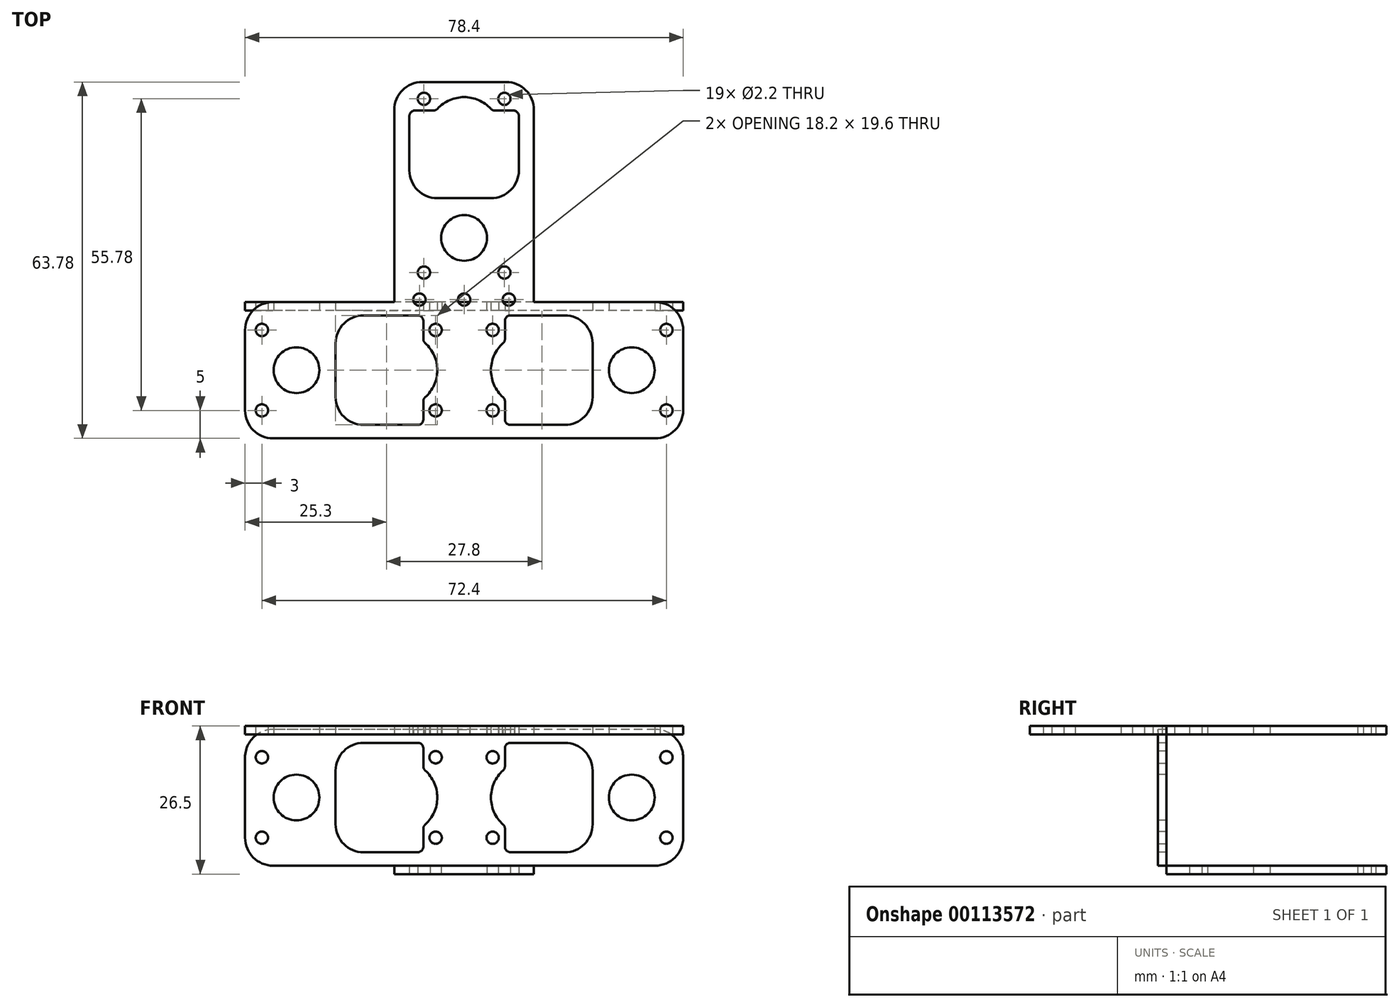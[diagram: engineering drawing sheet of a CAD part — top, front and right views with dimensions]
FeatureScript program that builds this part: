
annotation { "Feature Type Name" : "Feature", "Feature Type Description" : "" }
export const myFeature = defineFeature(function(context is Context, id is Id, definition is map)
    precondition{}
    {
        {
            var Q0;
            Q0=qCreatedBy(makeId("Top.planeOp"),FACE);
            var sketch = newSketch(context, id + "F0", { "sketchPlane" : qUnion([Q0])});
            skLineSegment(sketch, "E0.bottom", {"start": v(39.2, -12.2) * mm, "end": v(-39.2, -12.2) * mm});
            skLineSegment(sketch, "E0.top", {"start": v(39.2, 12.2) * mm, "end": v(-39.2, 12.2) * mm});
            skLineSegment(sketch, "E0.left", {"start": v(39.2, -12.2) * mm, "end": v(39.2, 12.2) * mm});
            skLineSegment(sketch, "E0.right", {"start": v(-39.2, -12.2) * mm, "end": v(-39.2, 12.2) * mm});
            skPoint(sketch, "E0.middle", {"position": v(0, 0) * mm});
            skCircle(sketch, "E1", {"center": v(-30, 0) * mm, "radius": 4.1 * mm});
            skCircle(sketch, "E2", {"center": v(-36.2, 7.2) * mm, "radius": 1.1 * mm});
            skCircle(sketch, "E3", {"center": v(-5.1, 7.2) * mm, "radius": 1.1 * mm});
            skLineSegment(sketch, "E4.bottom", {"start": v(-18, 9.8) * mm, "end": v(-8.3, 9.8) * mm});
            skLineSegment(sketch, "E4.top", {"start": v(-18, -9.8) * mm, "end": v(-8.3, -9.8) * mm});
            skLineSegment(sketch, "E4.left", {"start": v(-23, 4.8) * mm, "end": v(-23, -4.8) * mm});
            skLineSegment(sketch, "E4.right", {"start": v(-7.3, 8.8) * mm, "end": v(-7.3, 5.6) * mm});
            skPoint(sketch, "E4.middle", {"position": v(-15.15, 0) * mm});
            skPoint(sketch, "E5.visualSharp", {"position": v(-23, 9.8) * mm});
            skArc(sketch, "E5.filletArc", {"start": v(-18, 9.8) * mm, "mid": v(-21.54, 8.34) * mm, "end": v(-23, 4.8) * mm});
            skPoint(sketch, "E6.visualSharp", {"position": v(-23, -9.8) * mm});
            skArc(sketch, "E6.filletArc", {"start": v(-23, -4.8) * mm, "mid": v(-21.54, -8.34) * mm, "end": v(-18, -9.8) * mm});
            skPoint(sketch, "E7.visualSharp", {"position": v(-7.3, 9.8) * mm});
            skArc(sketch, "E7.filletArc", {"start": v(-7.3, 8.8) * mm, "mid": v(-7.6, 9.5) * mm, "end": v(-8.3, 9.8) * mm});
            skPoint(sketch, "E8.visualSharp", {"position": v(-7.3, -9.8) * mm});
            skArc(sketch, "E8.filletArc", {"start": v(-8.3, -9.8) * mm, "mid": v(-7.6, -9.5) * mm, "end": v(-7.3, -8.8) * mm});
            skCircle(sketch, "E9.MirrorC", {"center": v(-36.2, -7.2) * mm, "radius": 1.1 * mm});
            skCircle(sketch, "E10.MirrorC", {"center": v(-5.1, -7.2) * mm, "radius": 1.1 * mm});
            skArc(sketch, "E11.MirrorCS", {"start": v(7.3, 8.8) * mm, "mid": v(7.6, 9.5) * mm, "end": v(8.3, 9.8) * mm});
            skArc(sketch, "E12.MirrorCS", {"start": v(8.3, -9.8) * mm, "mid": v(7.6, -9.5) * mm, "end": v(7.3, -8.8) * mm});
            skCircle(sketch, "E13.MirrorC", {"center": v(5.1, -7.2) * mm, "radius": 1.1 * mm});
            skArc(sketch, "E14.MirrorCS", {"start": v(23, -4.8) * mm, "mid": v(21.54, -8.34) * mm, "end": v(18, -9.8) * mm});
            skArc(sketch, "E15.MirrorCS", {"start": v(18, 9.8) * mm, "mid": v(21.54, 8.34) * mm, "end": v(23, 4.8) * mm});
            skLineSegment(sketch, "E16.MirrorCS", {"start": v(7.3, 8.8) * mm, "end": v(7.3, 5.6) * mm});
            skPoint(sketch, "E17.MirrorP", {"position": v(7.3, -9.8) * mm});
            skLineSegment(sketch, "E18.MirrorCS", {"start": v(18, 9.8) * mm, "end": v(8.3, 9.8) * mm});
            skCircle(sketch, "E19.MirrorC", {"center": v(5.1, 7.2) * mm, "radius": 1.1 * mm});
            skPoint(sketch, "E20.MirrorP", {"position": v(7.3, 9.8) * mm});
            skPoint(sketch, "E21.MirrorP", {"position": v(15.15, 0) * mm});
            skCircle(sketch, "E22.MirrorC", {"center": v(36.2, -7.2) * mm, "radius": 1.1 * mm});
            skCircle(sketch, "E23.MirrorC", {"center": v(36.2, 7.2) * mm, "radius": 1.1 * mm});
            skCircle(sketch, "E24.MirrorC", {"center": v(30, 0) * mm, "radius": 4.1 * mm});
            skLineSegment(sketch, "E25.MirrorCS", {"start": v(23, 4.8) * mm, "end": v(23, -4.8) * mm});
            skPoint(sketch, "E26.MirrorP", {"position": v(23, -9.8) * mm});
            skLineSegment(sketch, "E27.MirrorCS", {"start": v(18, -9.8) * mm, "end": v(8.3, -9.8) * mm});
            skPoint(sketch, "E28.MirrorP", {"position": v(23, 9.8) * mm});
            skArc(sketch, "E29", {"start": v(-6.97, -4.84) * mm, "mid": v(-4.8, 0) * mm, "end": v(-6.97, 4.84) * mm});
            skLineSegment(sketch, "E30.trimOffspring", {"start": v(-7.3, -5.6) * mm, "end": v(-7.3, -8.8) * mm});
            skPoint(sketch, "E31.visualSharp", {"position": v(-7.3, 5.12) * mm});
            skArc(sketch, "E31.filletArc", {"start": v(-7.3, 5.6) * mm, "mid": v(-7.21, 5.18) * mm, "end": v(-6.97, 4.84) * mm});
            skPoint(sketch, "E32.visualSharp", {"position": v(-7.3, -5.12) * mm});
            skArc(sketch, "E32.filletArc", {"start": v(-6.97, -4.84) * mm, "mid": v(-7.21, -5.18) * mm, "end": v(-7.3, -5.6) * mm});
            skArc(sketch, "E33.MirrorCS", {"start": v(7.3, 5.6) * mm, "mid": v(7.21, 5.18) * mm, "end": v(6.97, 4.84) * mm});
            skArc(sketch, "E34.MirrorCS", {"start": v(6.97, -4.84) * mm, "mid": v(4.8, 0) * mm, "end": v(6.97, 4.84) * mm});
            skPoint(sketch, "E35.MirrorP", {"position": v(7.3, 5.12) * mm});
            skPoint(sketch, "E36.MirrorP", {"position": v(7.3, -5.12) * mm});
            skArc(sketch, "E37.MirrorCS", {"start": v(6.97, -4.84) * mm, "mid": v(7.21, -5.18) * mm, "end": v(7.3, -5.6) * mm});
            skLineSegment(sketch, "E38.trimOffspring", {"start": v(7.3, -5.6) * mm, "end": v(7.3, -8.8) * mm});
            skSolve(sketch);
        }
        {
            var Q0;
            Q0=qSketchRegion(id+"F0",true);
            extrude(context, id + "F1", {"entities" : qUnion([Q0]), "depth" : 1.5 * mm});
        }
        {
            var Q0;
            Q0=qCreatedBy(makeId("Top.planeOp"),FACE);
            var sketch = newSketch(context, id + "F2", { "sketchPlane" : qUnion([Q0])});
            skLineSegment(sketch, "E39.bottom", {"start": v(12.5, 12.2) * mm, "end": v(-12.5, 12.2) * mm});
            skLineSegment(sketch, "E39.top", {"start": v(12.5, 13.7) * mm, "end": v(-12.5, 13.7) * mm});
            skLineSegment(sketch, "E39.left", {"start": v(12.5, 12.2) * mm, "end": v(12.5, 13.7) * mm});
            skLineSegment(sketch, "E39.right", {"start": v(-12.5, 12.2) * mm, "end": v(-12.5, 13.7) * mm});
            skPoint(sketch, "E39.middle", {"position": v(0, 12.95) * mm});
            skLineSegment(sketch, "E40.0", {"start": v(39.2, 12.2) * mm, "end": v(-39.2, 12.2) * mm, "construction": true});
            skSolve(sketch);
        }
        {
            var Q0;
            Q0=qSketchRegion(id+"F2",true);
            extrude(context, id + "F3", {"entities" : qUnion([Q0]), "operationType" : NewBodyOperationType.ADD, "depth" : (40 + 0.44 * 2) * mm});
        }
        {
            var Q0;
            Q0=makeQuery(id+"F3.opExtrude","SWEPT_FACE",FACE,{"disambiguationData":[OSD([sQuery(id+"F2.wireOp",EDGE,"E39.top")])]});
            var sketch = newSketch(context, id + "F4", { "sketchPlane" : qUnion([Q0])});
            skLineSegment(sketch, "E41", {"start": v(-12.5, 20.44) * mm, "end": v(12.5, 20.44) * mm, "construction": true});
            skCircle(sketch, "E42", {"center": v(7.2, 37.88) * mm, "radius": 1.1 * mm});
            skCircle(sketch, "E43", {"center": v(7.2, 6.78) * mm, "radius": 1.1 * mm});
            skCircle(sketch, "E44", {"center": v(0, 12.98) * mm, "radius": 4.1 * mm});
            skLineSegment(sketch, "E45.bottom", {"start": v(8.8, 35.78) * mm, "end": v(5.5, 35.78) * mm});
            skLineSegment(sketch, "E45.top", {"start": v(4.8, 20.08) * mm, "end": v(-4.8, 20.08) * mm});
            skLineSegment(sketch, "E45.left", {"start": v(9.8, 34.78) * mm, "end": v(9.8, 25.08) * mm});
            skLineSegment(sketch, "E45.right", {"start": v(-9.8, 34.78) * mm, "end": v(-9.8, 25.08) * mm});
            skPoint(sketch, "E45.middle", {"position": v(0, 27.93) * mm});
            skPoint(sketch, "E46.visualSharp", {"position": v(-9.8, 20.08) * mm});
            skArc(sketch, "E46.filletArc", {"start": v(-9.8, 25.08) * mm, "mid": v(-8.34, 21.54) * mm, "end": v(-4.8, 20.08) * mm});
            skPoint(sketch, "E47.visualSharp", {"position": v(9.8, 20.08) * mm});
            skArc(sketch, "E47.filletArc", {"start": v(4.8, 20.08) * mm, "mid": v(8.34, 21.54) * mm, "end": v(9.8, 25.08) * mm});
            skPoint(sketch, "E48.visualSharp", {"position": v(9.8, 35.78) * mm});
            skArc(sketch, "E48.filletArc", {"start": v(9.8, 34.78) * mm, "mid": v(9.5, 35.49) * mm, "end": v(8.8, 35.78) * mm});
            skPoint(sketch, "E49.visualSharp", {"position": v(-9.8, 35.78) * mm});
            skArc(sketch, "E49.filletArc", {"start": v(-8.8, 35.78) * mm, "mid": v(-9.5, 35.49) * mm, "end": v(-9.8, 34.78) * mm});
            skCircle(sketch, "E50.MirrorC", {"center": v(-7.2, 37.88) * mm, "radius": 1.1 * mm});
            skCircle(sketch, "E51.MirrorC", {"center": v(-7.2, 6.78) * mm, "radius": 1.1 * mm});
            skArc(sketch, "E52", {"start": v(4.77, 36.1) * mm, "mid": v(0, 38.18) * mm, "end": v(-4.77, 36.1) * mm});
            skLineSegment(sketch, "E53.trimOffspring", {"start": v(-5.5, 35.78) * mm, "end": v(-8.8, 35.78) * mm});
            skPoint(sketch, "E54.visualSharp", {"position": v(-5.04, 35.78) * mm});
            skArc(sketch, "E54.filletArc", {"start": v(-5.5, 35.78) * mm, "mid": v(-5.1, 35.86) * mm, "end": v(-4.77, 36.1) * mm});
            skPoint(sketch, "E55.visualSharp", {"position": v(5.04, 35.78) * mm});
            skArc(sketch, "E55.filletArc", {"start": v(4.77, 36.1) * mm, "mid": v(5.1, 35.86) * mm, "end": v(5.5, 35.78) * mm});
            skSolve(sketch);
        }
        {
            var Q0;
            Q0=qSketchRegion(id+"F4",true);
            extrude(context, id + "F5", {"entities" : qUnion([Q0]), "operationType" : NewBodyOperationType.REMOVE, "endBound" : BoundingType.UP_TO_NEXT, "oppositeDirection" : true, "depth" : 25 * mm});
        }
        {
            var Q0;
            Q0=makeQuery(id+"F1.opExtrude","SWEPT_EDGE",EDGE,{"disambiguationData":[OSD([sQuery(id+"F0.wireOp",EDGE,"E0.top"),sQuery(id+"F0.wireOp",EDGE,"E0.right")])]});
            var Q1;
            Q1=makeQuery(id+"F1.opExtrude","SWEPT_EDGE",EDGE,{"disambiguationData":[OSD([sQuery(id+"F0.wireOp",EDGE,"E0.bottom"),sQuery(id+"F0.wireOp",EDGE,"E0.right")])]});
            var Q2;
            Q2=makeQuery(id+"F1.opExtrude","SWEPT_EDGE",EDGE,{"disambiguationData":[OSD([sQuery(id+"F0.wireOp",EDGE,"E0.top"),sQuery(id+"F0.wireOp",EDGE,"E0.left")])]});
            var Q3;
            Q3=makeQuery(id+"F1.opExtrude","SWEPT_EDGE",EDGE,{"disambiguationData":[OSD([sQuery(id+"F0.wireOp",EDGE,"E0.bottom"),sQuery(id+"F0.wireOp",EDGE,"E0.left")])]});
            var Q4;
            Q4=makeQuery(id+"F3.opExtrude","CAP_EDGE",EDGE,{"disambiguationData":[OSD([sQuery(id+"F2.wireOp",EDGE,"E39.right")])],"isStart":false});
            var Q5;
            Q5=makeQuery(id+"F3.opExtrude","CAP_EDGE",EDGE,{"disambiguationData":[OSD([sQuery(id+"F2.wireOp",EDGE,"E39.left")])],"isStart":false});
            fillet(context, id + "F6", {"entities" : qUnion([Q0, Q1, Q2, Q3, Q4, Q5]), "radius" : 5 * mm, "tangentPropagation" : true, "allowEdgeOverflow" : false});
        }
        {
            var Q0;
            Q0=makeQuery(id+"F3.opExtrude","SWEPT_FACE",FACE,{"disambiguationData":[OSD([sQuery(id+"F2.wireOp",EDGE,"E39.left")])]});
            var sketch = newSketch(context, id + "F7", { "sketchPlane" : qUnion([Q0])});
            skLineSegment(sketch, "E56.bottom", {"start": v(12.2, 1.5) * mm, "end": v(13.7, 1.5) * mm});
            skLineSegment(sketch, "E56.top", {"start": v(12.2, 0) * mm, "end": v(13.7, 0) * mm});
            skLineSegment(sketch, "E56.left", {"start": v(12.2, 1.5) * mm, "end": v(12.2, 0) * mm});
            skLineSegment(sketch, "E56.right", {"start": v(13.7, 1.5) * mm, "end": v(13.7, 0) * mm});
            skSolve(sketch);
        }
        {
            var Q0;
            Q0 = qSketchRegion(id + "F7", true);
            extrude(context, id + "F8", {"entities" : qUnion([Q0]), "operationType" : NewBodyOperationType.REMOVE, "endBound" : BoundingType.THROUGH_ALL, "oppositeDirection" : true, "depth" : 25 * mm});
        }
        {
            var Q0;
            Q0=makeQuery(id+"F8.boolean.opBoolean","SPLIT",BODY,{"disambiguationData":[OD(1.0)],"derivedFrom":makeQuery(id+"F1.opExtrude","SWEPT_BODY",BODY,{"disambiguationData":[OSD([sQuery(id+"F0.wireOp",EDGE,"E0.bottom"),sQuery(id+"F0.wireOp",EDGE,"E0.top"),sQuery(id+"F0.wireOp",EDGE,"E0.left"),sQuery(id+"F0.wireOp",EDGE,"E0.right"),sQuery(id+"F0.wireOp",EDGE,"E1"),sQuery(id+"F0.wireOp",EDGE,"E2"),sQuery(id+"F0.wireOp",EDGE,"E3"),sQuery(id+"F0.wireOp",EDGE,"E4.bottom"),sQuery(id+"F0.wireOp",EDGE,"E4.top"),sQuery(id+"F0.wireOp",EDGE,"E4.left"),sQuery(id+"F0.wireOp",EDGE,"E4.right"),sQuery(id+"F0.wireOp",EDGE,"E5.filletArc"),sQuery(id+"F0.wireOp",EDGE,"E6.filletArc"),sQuery(id+"F0.wireOp",EDGE,"E7.filletArc"),sQuery(id+"F0.wireOp",EDGE,"E8.filletArc"),sQuery(id+"F0.wireOp",EDGE,"E9.MirrorC"),sQuery(id+"F0.wireOp",EDGE,"E10.MirrorC"),sQuery(id+"F0.wireOp",EDGE,"E11.MirrorCS"),sQuery(id+"F0.wireOp",EDGE,"E12.MirrorCS"),sQuery(id+"F0.wireOp",EDGE,"E13.MirrorC"),sQuery(id+"F0.wireOp",EDGE,"E14.MirrorCS"),sQuery(id+"F0.wireOp",EDGE,"E15.MirrorCS"),sQuery(id+"F0.wireOp",EDGE,"E16.MirrorCS"),sQuery(id+"F0.wireOp",EDGE,"E18.MirrorCS"),sQuery(id+"F0.wireOp",EDGE,"E19.MirrorC"),sQuery(id+"F0.wireOp",EDGE,"E22.MirrorC"),sQuery(id+"F0.wireOp",EDGE,"E23.MirrorC"),sQuery(id+"F0.wireOp",EDGE,"E24.MirrorC"),sQuery(id+"F0.wireOp",EDGE,"E25.MirrorCS"),sQuery(id+"F0.wireOp",EDGE,"E27.MirrorCS"),sQuery(id+"F0.wireOp",EDGE,"E29"),sQuery(id+"F0.wireOp",EDGE,"E30.trimOffspring"),sQuery(id+"F0.wireOp",EDGE,"E31.filletArc"),sQuery(id+"F0.wireOp",EDGE,"E32.filletArc"),sQuery(id+"F0.wireOp",EDGE,"E33.MirrorCS"),sQuery(id+"F0.wireOp",EDGE,"E34.MirrorCS"),sQuery(id+"F0.wireOp",EDGE,"E37.MirrorCS"),sQuery(id+"F0.wireOp",EDGE,"E38.trimOffspring")])]})});
            var Q1;
            {var subQ0=sQuery(id+"F2.wireOp",EDGE,"E39.left");var subQ1=sQuery(id+"F2.wireOp",EDGE,"E39.bottom");var subQ2=makeQuery(id+"F3.opExtrude","SWEPT_FACE",FACE,{"disambiguationData":[OSD([subQ1])]});var subQ3=sQuery(id+"F0.wireOp",EDGE,"E0.right");var subQ4=sQuery(id+"F0.wireOp",EDGE,"E0.top");var subQ5=makeQuery(id+"F1.opExtrude","SWEPT_FACE",FACE,{"disambiguationData":[OSD([subQ4])]});var subQ6=sQuery(id+"F0.wireOp",EDGE,"E0.left");var subQ7=makeQuery(id+"F1.opExtrude","CAP_FACE",FACE,{"disambiguationData":[OSD([sQuery(id+"F0.wireOp",EDGE,"E0.bottom"),subQ4,subQ6,subQ3,sQuery(id+"F0.wireOp",EDGE,"E1"),sQuery(id+"F0.wireOp",EDGE,"E2"),sQuery(id+"F0.wireOp",EDGE,"E3"),sQuery(id+"F0.wireOp",EDGE,"E4.bottom"),sQuery(id+"F0.wireOp",EDGE,"E4.top"),sQuery(id+"F0.wireOp",EDGE,"E4.left"),sQuery(id+"F0.wireOp",EDGE,"E4.right"),sQuery(id+"F0.wireOp",EDGE,"E5.filletArc"),sQuery(id+"F0.wireOp",EDGE,"E6.filletArc"),sQuery(id+"F0.wireOp",EDGE,"E7.filletArc"),sQuery(id+"F0.wireOp",EDGE,"E8.filletArc"),sQuery(id+"F0.wireOp",EDGE,"E9.MirrorC"),sQuery(id+"F0.wireOp",EDGE,"E10.MirrorC"),sQuery(id+"F0.wireOp",EDGE,"E11.MirrorCS"),sQuery(id+"F0.wireOp",EDGE,"E12.MirrorCS"),sQuery(id+"F0.wireOp",EDGE,"E13.MirrorC"),sQuery(id+"F0.wireOp",EDGE,"E14.MirrorCS"),sQuery(id+"F0.wireOp",EDGE,"E15.MirrorCS"),sQuery(id+"F0.wireOp",EDGE,"E16.MirrorCS"),sQuery(id+"F0.wireOp",EDGE,"E18.MirrorCS"),sQuery(id+"F0.wireOp",EDGE,"E19.MirrorC"),sQuery(id+"F0.wireOp",EDGE,"E22.MirrorC"),sQuery(id+"F0.wireOp",EDGE,"E23.MirrorC"),sQuery(id+"F0.wireOp",EDGE,"E24.MirrorC"),sQuery(id+"F0.wireOp",EDGE,"E25.MirrorCS"),sQuery(id+"F0.wireOp",EDGE,"E27.MirrorCS"),sQuery(id+"F0.wireOp",EDGE,"E29"),sQuery(id+"F0.wireOp",EDGE,"E30.trimOffspring"),sQuery(id+"F0.wireOp",EDGE,"E31.filletArc"),sQuery(id+"F0.wireOp",EDGE,"E32.filletArc"),sQuery(id+"F0.wireOp",EDGE,"E33.MirrorCS"),sQuery(id+"F0.wireOp",EDGE,"E34.MirrorCS"),sQuery(id+"F0.wireOp",EDGE,"E37.MirrorCS"),sQuery(id+"F0.wireOp",EDGE,"E38.trimOffspring")])],"isStart":false});var subQ8=makeQuery(id+"F3.opExtrude","SWEPT_FACE",FACE,{"disambiguationData":[OSD([sQuery(id+"F2.wireOp",EDGE,"E39.right")])]});var subQ9=makeQuery(id+"F1.opExtrude","CAP_EDGE",EDGE,{"disambiguationData":[OSD([subQ4])],"isStart":false});var subQ10=makeQuery(id+"F3.opExtrude","SWEPT_FACE",FACE,{"disambiguationData":[OSD([subQ0])]});Q1=makeQuery(id+"F8.boolean.opBoolean","MERGE",EDGE,{"derivedFrom":[makeQuery(id+"F3.boolean.opBoolean","SPLIT",EDGE,{"disambiguationData":[TD([subQ7,subQ5,subQ2,subQ10,subQ8])],"derivedFrom":subQ9}),makeQuery(id+"F3.boolean.opBoolean","SPLIT",EDGE,{"disambiguationData":[TD([subQ7,subQ5,makeQuery(id+"F1.opExtrude","SWEPT_FACE",FACE,{"disambiguationData":[OSD([subQ6])]}),subQ2,subQ10])],"derivedFrom":subQ9}),makeQuery(id+"F3.boolean.opBoolean","SPLIT",EDGE,{"disambiguationData":[TD([subQ7,subQ5,makeQuery(id+"F1.opExtrude","SWEPT_FACE",FACE,{"disambiguationData":[OSD([subQ3])]}),subQ2,subQ8])],"derivedFrom":subQ9}),makeQuery(id+"F8.opExtrude","SWEPT_EDGE",EDGE,{"disambiguationData":[OSD([subQ1,subQ0,sQuery(id+"F7.wireOp",EDGE,"E56.bottom"),sQuery(id+"F7.wireOp",EDGE,"E56.left")])]})]});}
            transform(context, id + "F9", {"entities" : qUnion([Q0]), "transformType" : TransformType.ROTATION, "transformAxis" : qUnion([Q1]), "angle" : 90 * degree, "makeCopy" : false});
        }
        {
            var Q0;
            Q0=qCreatedBy(makeId("Top.planeOp"),FACE);
            cPlane(context, id + "F10", {"entities" : qUnion([Q0]), "cplaneType" : CPlaneType.OFFSET, "offset" : 25 * mm, "width" : 150 * mm, "height" : 150 * mm});
        }
        {
            var Q0;
            Q0=qCreatedBy(id+"F10.planeOp",FACE);
            var sketch = newSketch(context, id + "F11", { "sketchPlane" : qUnion([Q0])});
            skLineSegment(sketch, "E57.0", {"start": v(34.2, 12.2) * mm, "end": v(12.5, 12.2) * mm});
            skArc(sketch, "E58.0", {"start": v(-34.2, 12.2) * mm, "mid": v(-37.74, 10.74) * mm, "end": v(-39.2, 7.2) * mm});
            skLineSegment(sketch, "E59.0", {"start": v(-39.2, -7.2) * mm, "end": v(-39.2, 7.2) * mm});
            skArc(sketch, "E60.0", {"start": v(-39.2, -7.2) * mm, "mid": v(-37.74, -10.74) * mm, "end": v(-34.2, -12.2) * mm});
            skLineSegment(sketch, "E61.0", {"start": v(34.2, -12.2) * mm, "end": v(-34.2, -12.2) * mm});
            skCircle(sketch, "E62.0", {"center": v(-36.2, -7.2) * mm, "radius": 1.1 * mm});
            skCircle(sketch, "E63.0", {"center": v(-36.2, 7.2) * mm, "radius": 1.1 * mm});
            skCircle(sketch, "E64.0", {"center": v(-30, 0) * mm, "radius": 4.1 * mm});
            skArc(sketch, "E65.0", {"start": v(-18, 9.8) * mm, "mid": v(-21.54, 8.34) * mm, "end": v(-23, 4.8) * mm});
            skLineSegment(sketch, "E66.0", {"start": v(-23, 4.8) * mm, "end": v(-23, -4.8) * mm});
            skArc(sketch, "E67.0", {"start": v(-23, -4.8) * mm, "mid": v(-21.54, -8.34) * mm, "end": v(-18, -9.8) * mm});
            skLineSegment(sketch, "E68.0", {"start": v(-18, -9.8) * mm, "end": v(-8.3, -9.8) * mm});
            skLineSegment(sketch, "E69.0", {"start": v(-18, 9.8) * mm, "end": v(-8.3, 9.8) * mm});
            skArc(sketch, "E70.0", {"start": v(-7.3, 8.8) * mm, "mid": v(-7.6, 9.5) * mm, "end": v(-8.3, 9.8) * mm});
            skLineSegment(sketch, "E71.0", {"start": v(-7.3, 8.8) * mm, "end": v(-7.3, 5.6) * mm});
            skArc(sketch, "E72.0", {"start": v(-7.3, 5.6) * mm, "mid": v(-7.21, 5.18) * mm, "end": v(-6.97, 4.84) * mm});
            skArc(sketch, "E73.0", {"start": v(-8.3, -9.8) * mm, "mid": v(-7.6, -9.5) * mm, "end": v(-7.3, -8.8) * mm});
            skLineSegment(sketch, "E74.0", {"start": v(-7.3, -5.6) * mm, "end": v(-7.3, -8.8) * mm});
            skArc(sketch, "E75.0", {"start": v(-6.97, -4.84) * mm, "mid": v(-7.21, -5.18) * mm, "end": v(-7.3, -5.6) * mm});
            skArc(sketch, "E76.0", {"start": v(-6.97, -4.84) * mm, "mid": v(-4.8, 0) * mm, "end": v(-6.97, 4.84) * mm});
            skCircle(sketch, "E77.0", {"center": v(-5.1, 7.2) * mm, "radius": 1.1 * mm});
            skCircle(sketch, "E78.0", {"center": v(-5.1, -7.2) * mm, "radius": 1.1 * mm});
            skArc(sketch, "E79.MirrorCS", {"start": v(6.97, -4.84) * mm, "mid": v(7.21, -5.18) * mm, "end": v(7.3, -5.6) * mm});
            skArc(sketch, "E80.MirrorCS", {"start": v(7.3, 5.6) * mm, "mid": v(7.21, 5.18) * mm, "end": v(6.97, 4.84) * mm});
            skLineSegment(sketch, "E81.MirrorCS", {"start": v(23, 4.8) * mm, "end": v(23, -4.8) * mm});
            skArc(sketch, "E82.MirrorCS", {"start": v(23, -4.8) * mm, "mid": v(21.54, -8.34) * mm, "end": v(18, -9.8) * mm});
            skArc(sketch, "E83.MirrorCS", {"start": v(18, 9.8) * mm, "mid": v(21.54, 8.34) * mm, "end": v(23, 4.8) * mm});
            skCircle(sketch, "E84.MirrorC", {"center": v(30, 0) * mm, "radius": 4.1 * mm});
            skLineSegment(sketch, "E85.MirrorCS", {"start": v(18, -9.8) * mm, "end": v(8.3, -9.8) * mm});
            skLineSegment(sketch, "E86.MirrorCS", {"start": v(18, 9.8) * mm, "end": v(8.3, 9.8) * mm});
            skCircle(sketch, "E87.MirrorC", {"center": v(36.2, 7.2) * mm, "radius": 1.1 * mm});
            skCircle(sketch, "E88.MirrorC", {"center": v(36.2, -7.2) * mm, "radius": 1.1 * mm});
            skArc(sketch, "E89.MirrorCS", {"start": v(8.3, -9.8) * mm, "mid": v(7.6, -9.5) * mm, "end": v(7.3, -8.8) * mm});
            skArc(sketch, "E90.MirrorCS", {"start": v(39.2, -7.2) * mm, "mid": v(37.74, -10.74) * mm, "end": v(34.2, -12.2) * mm});
            skArc(sketch, "E91.MirrorCS", {"start": v(6.97, -4.84) * mm, "mid": v(4.8, 0) * mm, "end": v(6.97, 4.84) * mm});
            skLineSegment(sketch, "E92.MirrorCS", {"start": v(7.3, -5.6) * mm, "end": v(7.3, -8.8) * mm});
            skLineSegment(sketch, "E93.MirrorCS", {"start": v(39.2, -7.2) * mm, "end": v(39.2, 7.2) * mm});
            skArc(sketch, "E94.MirrorCS", {"start": v(34.2, 12.2) * mm, "mid": v(37.74, 10.74) * mm, "end": v(39.2, 7.2) * mm});
            skCircle(sketch, "E95.MirrorC", {"center": v(5.1, 7.2) * mm, "radius": 1.1 * mm});
            skCircle(sketch, "E96.MirrorC", {"center": v(5.1, -7.2) * mm, "radius": 1.1 * mm});
            skLineSegment(sketch, "E97.MirrorCS", {"start": v(7.3, 8.8) * mm, "end": v(7.3, 5.6) * mm});
            skArc(sketch, "E98.MirrorCS", {"start": v(7.3, 8.8) * mm, "mid": v(7.6, 9.5) * mm, "end": v(8.3, 9.8) * mm});
            skLineSegment(sketch, "E99.0", {"start": v(-12.5, 46.58) * mm, "end": v(-12.5, 12.2) * mm});
            skLineSegment(sketch, "E100.0", {"start": v(12.5, 46.58) * mm, "end": v(12.5, 12.2) * mm});
            skArc(sketch, "E101.0", {"start": v(-7.5, 51.58) * mm, "mid": v(-11.04, 50.12) * mm, "end": v(-12.5, 46.58) * mm});
            skLineSegment(sketch, "E102.0", {"start": v(7.5, 51.58) * mm, "end": v(-7.5, 51.58) * mm});
            skArc(sketch, "E103.0", {"start": v(12.5, 46.58) * mm, "mid": v(11.04, 50.12) * mm, "end": v(7.5, 51.58) * mm});
            skCircle(sketch, "E104.0", {"center": v(7.2, 48.58) * mm, "radius": 1.1 * mm});
            skCircle(sketch, "E105.0", {"center": v(-7.2, 48.58) * mm, "radius": 1.1 * mm});
            skCircle(sketch, "E106.0", {"center": v(-7.2, 17.48) * mm, "radius": 1.1 * mm});
            skCircle(sketch, "E107.0", {"center": v(7.2, 17.48) * mm, "radius": 1.1 * mm});
            skCircle(sketch, "E108.0", {"center": v(0, 23.68) * mm, "radius": 4.1 * mm});
            skLineSegment(sketch, "E109.0", {"start": v(-4.8, 30.78) * mm, "end": v(4.8, 30.78) * mm});
            skArc(sketch, "E110.0", {"start": v(9.8, 35.78) * mm, "mid": v(8.34, 32.24) * mm, "end": v(4.8, 30.78) * mm});
            skArc(sketch, "E111.0", {"start": v(-4.8, 30.78) * mm, "mid": v(-8.34, 32.24) * mm, "end": v(-9.8, 35.78) * mm});
            skLineSegment(sketch, "E112.0", {"start": v(-9.8, 45.48) * mm, "end": v(-9.8, 35.78) * mm});
            skLineSegment(sketch, "E113.0", {"start": v(9.8, 45.48) * mm, "end": v(9.8, 35.78) * mm});
            skArc(sketch, "E114.0", {"start": v(-4.77, 46.8) * mm, "mid": v(0, 48.88) * mm, "end": v(4.77, 46.8) * mm});
            skArc(sketch, "E115.0", {"start": v(-9.8, 45.48) * mm, "mid": v(-9.5, 46.19) * mm, "end": v(-8.8, 46.48) * mm});
            skLineSegment(sketch, "E116.0", {"start": v(-8.8, 46.48) * mm, "end": v(-5.5, 46.48) * mm});
            skArc(sketch, "E117.0", {"start": v(-4.77, 46.8) * mm, "mid": v(-5.1, 46.56) * mm, "end": v(-5.5, 46.48) * mm});
            skArc(sketch, "E118.0", {"start": v(5.5, 46.48) * mm, "mid": v(5.1, 46.56) * mm, "end": v(4.77, 46.8) * mm});
            skLineSegment(sketch, "E119.0", {"start": v(5.5, 46.48) * mm, "end": v(8.8, 46.48) * mm});
            skArc(sketch, "E120.0", {"start": v(8.8, 46.48) * mm, "mid": v(9.5, 46.19) * mm, "end": v(9.8, 45.48) * mm});
            skLineSegment(sketch, "E121.trimOffspring", {"start": v(-12.5, 12.2) * mm, "end": v(-34.2, 12.2) * mm});
            skSolve(sketch);
        }
        {
            var Q0;
            Q0 = qSketchRegion(id + "F11", true);
            extrude(context, id + "F12", {"entities" : qUnion([Q0]), "depth" : 1.5 * mm});
        }
        {
            var Q0;
            Q0=makeQuery(id+"F12.opExtrude","CAP_FACE",FACE,{"disambiguationData":[OSD([sQuery(id+"F11.wireOp",EDGE,"E57.0"),sQuery(id+"F11.wireOp",EDGE,"E58.0"),sQuery(id+"F11.wireOp",EDGE,"E59.0"),sQuery(id+"F11.wireOp",EDGE,"E60.0"),sQuery(id+"F11.wireOp",EDGE,"E61.0"),sQuery(id+"F11.wireOp",EDGE,"E62.0"),sQuery(id+"F11.wireOp",EDGE,"E63.0"),sQuery(id+"F11.wireOp",EDGE,"E64.0"),sQuery(id+"F11.wireOp",EDGE,"E65.0"),sQuery(id+"F11.wireOp",EDGE,"E66.0"),sQuery(id+"F11.wireOp",EDGE,"E67.0"),sQuery(id+"F11.wireOp",EDGE,"E68.0"),sQuery(id+"F11.wireOp",EDGE,"E69.0"),sQuery(id+"F11.wireOp",EDGE,"E70.0"),sQuery(id+"F11.wireOp",EDGE,"E71.0"),sQuery(id+"F11.wireOp",EDGE,"E72.0"),sQuery(id+"F11.wireOp",EDGE,"E73.0"),sQuery(id+"F11.wireOp",EDGE,"E74.0"),sQuery(id+"F11.wireOp",EDGE,"E75.0"),sQuery(id+"F11.wireOp",EDGE,"E76.0"),sQuery(id+"F11.wireOp",EDGE,"E77.0"),sQuery(id+"F11.wireOp",EDGE,"E78.0"),sQuery(id+"F11.wireOp",EDGE,"E79.MirrorCS"),sQuery(id+"F11.wireOp",EDGE,"E80.MirrorCS"),sQuery(id+"F11.wireOp",EDGE,"E81.MirrorCS"),sQuery(id+"F11.wireOp",EDGE,"E82.MirrorCS"),sQuery(id+"F11.wireOp",EDGE,"E83.MirrorCS"),sQuery(id+"F11.wireOp",EDGE,"E84.MirrorC"),sQuery(id+"F11.wireOp",EDGE,"E85.MirrorCS"),sQuery(id+"F11.wireOp",EDGE,"E86.MirrorCS"),sQuery(id+"F11.wireOp",EDGE,"E87.MirrorC"),sQuery(id+"F11.wireOp",EDGE,"E88.MirrorC"),sQuery(id+"F11.wireOp",EDGE,"E89.MirrorCS"),sQuery(id+"F11.wireOp",EDGE,"E90.MirrorCS"),sQuery(id+"F11.wireOp",EDGE,"E91.MirrorCS"),sQuery(id+"F11.wireOp",EDGE,"E92.MirrorCS"),sQuery(id+"F11.wireOp",EDGE,"E93.MirrorCS"),sQuery(id+"F11.wireOp",EDGE,"E94.MirrorCS"),sQuery(id+"F11.wireOp",EDGE,"E95.MirrorC"),sQuery(id+"F11.wireOp",EDGE,"E96.MirrorC"),sQuery(id+"F11.wireOp",EDGE,"E97.MirrorCS"),sQuery(id+"F11.wireOp",EDGE,"E98.MirrorCS"),sQuery(id+"F11.wireOp",EDGE,"E99.0"),sQuery(id+"F11.wireOp",EDGE,"E100.0"),sQuery(id+"F11.wireOp",EDGE,"E101.0"),sQuery(id+"F11.wireOp",EDGE,"E102.0"),sQuery(id+"F11.wireOp",EDGE,"E103.0"),sQuery(id+"F11.wireOp",EDGE,"E104.0"),sQuery(id+"F11.wireOp",EDGE,"E105.0"),sQuery(id+"F11.wireOp",EDGE,"E106.0"),sQuery(id+"F11.wireOp",EDGE,"E107.0"),sQuery(id+"F11.wireOp",EDGE,"E108.0"),sQuery(id+"F11.wireOp",EDGE,"E109.0"),sQuery(id+"F11.wireOp",EDGE,"E110.0"),sQuery(id+"F11.wireOp",EDGE,"E111.0"),sQuery(id+"F11.wireOp",EDGE,"E112.0"),sQuery(id+"F11.wireOp",EDGE,"E113.0"),sQuery(id+"F11.wireOp",EDGE,"E114.0"),sQuery(id+"F11.wireOp",EDGE,"E115.0"),sQuery(id+"F11.wireOp",EDGE,"E116.0"),sQuery(id+"F11.wireOp",EDGE,"E117.0"),sQuery(id+"F11.wireOp",EDGE,"E118.0"),sQuery(id+"F11.wireOp",EDGE,"E119.0"),sQuery(id+"F11.wireOp",EDGE,"E120.0"),sQuery(id+"F11.wireOp",EDGE,"E121.trimOffspring")])],"isStart":false});
            var sketch = newSketch(context, id + "F13", { "sketchPlane" : qUnion([Q0])});
            skLineSegment(sketch, "E122", {"start": v(-12.5, 12.64) * mm, "end": v(12.5, 12.64) * mm, "construction": true});
            skCircle(sketch, "E123", {"center": v(-8, 12.64) * mm, "radius": 1.1 * mm});
            skCircle(sketch, "E124", {"center": v(0, 12.64) * mm, "radius": 1.1 * mm});
            skCircle(sketch, "E125.MirrorC", {"center": v(8, 12.64) * mm, "radius": 1.1 * mm});
            skSolve(sketch);
        }
        {
            var Q0;
            Q0 = qSketchRegion(id + "F13", true);
            extrude(context, id + "F14", {"entities" : qUnion([Q0]), "operationType" : NewBodyOperationType.REMOVE, "endBound" : BoundingType.UP_TO_NEXT, "oppositeDirection" : true, "depth" : 25 * mm});
        }
    });
